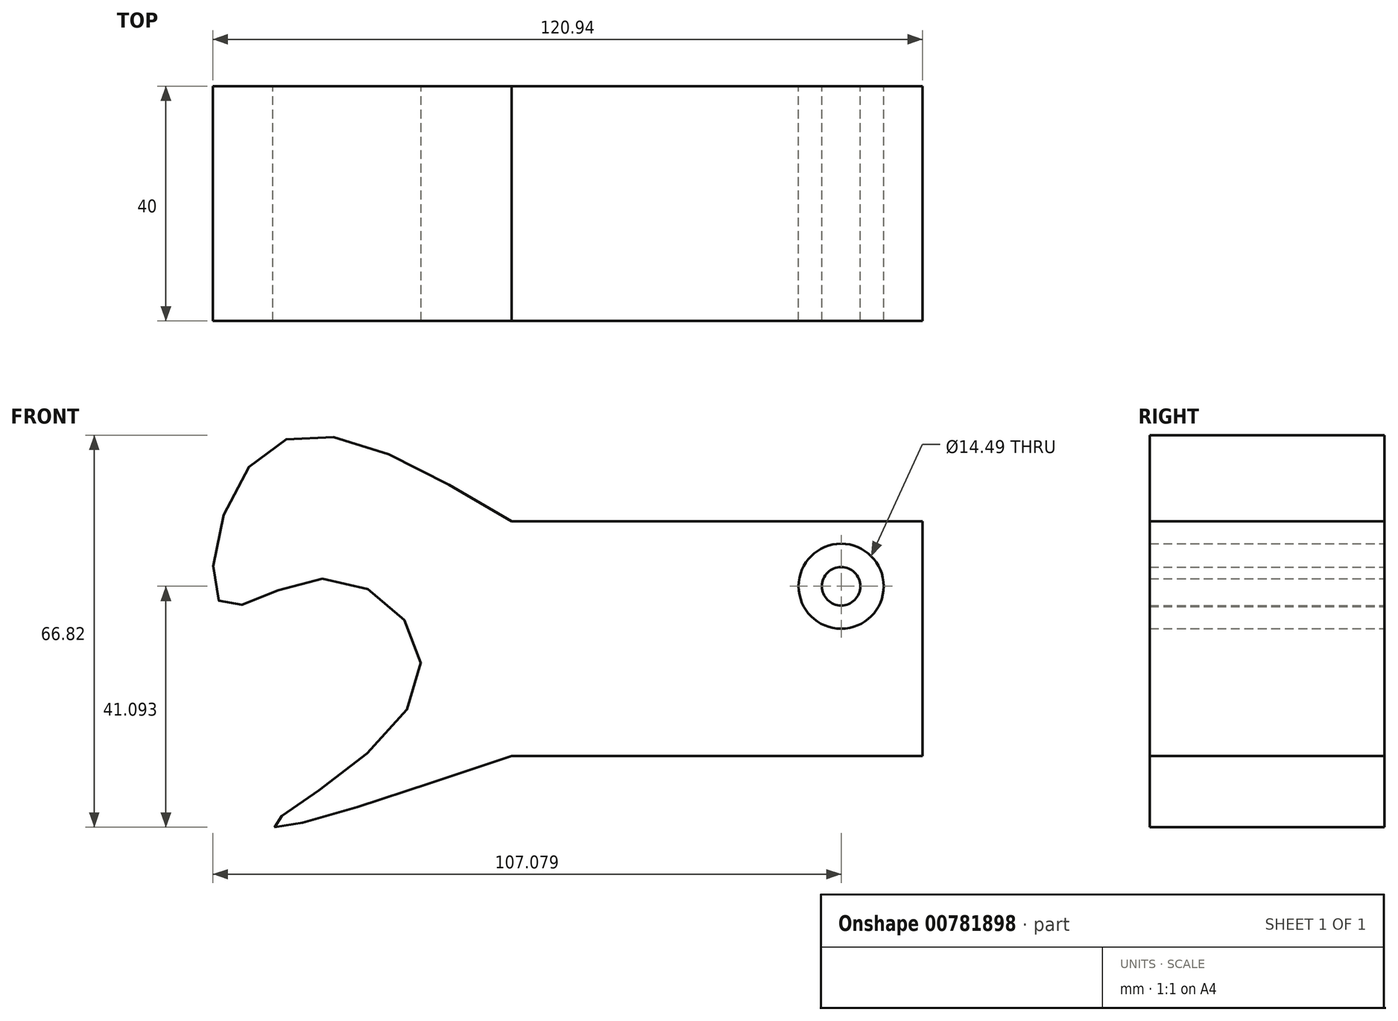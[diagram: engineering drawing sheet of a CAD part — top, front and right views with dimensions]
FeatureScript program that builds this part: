
annotation { "Feature Type Name" : "Feature", "Feature Type Description" : "" }
export const myFeature = defineFeature(function(context is Context, id is Id, definition is map)
    precondition{}
    {
        {
            var Q0;
            Q0=qCreatedBy(makeId("Front.planeOp"),FACE);
            var sketch = newSketch(context, id + "F0", { "sketchPlane" : qUnion([Q0])});
            skLineSegment(sketch, "E0.bottom", {"start": v(0, 40) * mm, "end": v(70, 40) * mm});
            skLineSegment(sketch, "E0.top", {"start": v(0, 0) * mm, "end": v(70, 0) * mm});
            skLineSegment(sketch, "E0.left", {"start": v(0, 40) * mm, "end": v(0, 0) * mm});
            skLineSegment(sketch, "E0.right", {"start": v(70, 40) * mm, "end": v(70, 0) * mm});
            skSolve(sketch);
        }
        {
            var Q0;
            Q0 = qSketchRegion(id + "F0", true);
            extrude(context, id + "F1", {"entities" : qUnion([Q0]), "depth" : 40 * mm, "offsetDistance" : 25 * mm});
        }
        {
            var Q0;
            Q0=makeQuery(id+"F1.opExtrude","CAP_FACE",FACE,{"disambiguationData":[OSD([sQuery(id+"F0.wireOp",EDGE,"E0.bottom"),sQuery(id+"F0.wireOp",EDGE,"E0.top"),sQuery(id+"F0.wireOp",EDGE,"E0.left"),sQuery(id+"F0.wireOp",EDGE,"E0.right")])],"isStart":true});
            var sketch = newSketch(context, id + "F2", { "sketchPlane" : qUnion([Q0])});
            skCircle(sketch, "E1", {"center": v(-49.98, 28.42) * mm, "radius": 9.73 * mm});
            skFitSpline(sketch, "E2", {"points": [v(0, 40) * mm, v(42.33, 51.89) * mm, v(49.56, 26.02) * mm, v(31.27, 30.23) * mm, v(15.95, 11.88) * mm, v(40.62, -11.58) * mm, v(0, 0) * mm], "startDerivative": vector(247.6, 148) * mm, "endDerivative": vector(-326, 109.93) * mm});
            skSolve(sketch);
        }
        {
            var Q0;
            Q0=makeQuery(id+"F2.imprint","IMPRINT",FACE,{"disambiguationData":[TD([[makeQuery(id+"F2.imprint","IMPRINT",EDGE,{"derivedFrom":sQuery(id+"F2.wireOp",EDGE,"E2")}),-1.0]])]});
            extrude(context, id + "F3", {"entities" : qUnion([Q0]), "operationType" : NewBodyOperationType.ADD, "oppositeDirection" : true, "depth" : 40 * mm, "offsetDistance" : 25 * mm});
        }
        {
            var Q0;
            {var subQ0=sQuery(id+"F0.wireOp",EDGE,"E0.left");Q0=makeQuery(id+"F3.boolean.opBoolean","MERGE",FACE,{"derivedFrom":[makeQuery(id+"F1.opExtrude","CAP_FACE",FACE,{"disambiguationData":[OSD([sQuery(id+"F0.wireOp",EDGE,"E0.bottom"),sQuery(id+"F0.wireOp",EDGE,"E0.top"),subQ0,sQuery(id+"F0.wireOp",EDGE,"E0.right")])],"isStart":true}),makeQuery(id+"F3.opExtrude","CAP_FACE",FACE,{"disambiguationData":[OSD([subQ0,sQuery(id+"F2.wireOp",EDGE,"E2")])],"isStart":true})]});}
            var sketch = newSketch(context, id + "F4", { "sketchPlane" : qUnion([Q0])});
            skCircle(sketch, "E3", {"center": v(-56.14, 28.93) * mm, "radius": 7.25 * mm});
            skSolve(sketch);
        }
        {
            var Q0;
            Q0 = qSketchRegion(id + "F4", true);
            extrude(context, id + "F5", {"entities" : qUnion([Q0]), "operationType" : NewBodyOperationType.REMOVE, "oppositeDirection" : true, "depth" : 110.5 * mm, "offsetDistance" : 25 * mm});
        }
        {
            var Q0;
            {var subQ0=sQuery(id+"F0.wireOp",EDGE,"E0.left");Q0=makeQuery(id+"F3.boolean.opBoolean","MERGE",FACE,{"derivedFrom":[makeQuery(id+"F1.opExtrude","CAP_FACE",FACE,{"disambiguationData":[OSD([sQuery(id+"F0.wireOp",EDGE,"E0.bottom"),sQuery(id+"F0.wireOp",EDGE,"E0.top"),subQ0,sQuery(id+"F0.wireOp",EDGE,"E0.right")])],"isStart":true}),makeQuery(id+"F3.opExtrude","CAP_FACE",FACE,{"disambiguationData":[OSD([subQ0,sQuery(id+"F2.wireOp",EDGE,"E2")])],"isStart":true})]});}
            var sketch = newSketch(context, id + "F6", { "sketchPlane" : qUnion([Q0])});
            skCircle(sketch, "E4", {"center": v(-56.14, 28.93) * mm, "radius": 3.28 * mm});
            skSolve(sketch);
        }
        {
            var Q0;
            Q0 = qSketchRegion(id + "F6", true);
            extrude(context, id + "F7", {"entities" : qUnion([Q0]), "oppositeDirection" : true, "depth" : 40 * mm, "offsetDistance" : 25 * mm});
        }
    });
